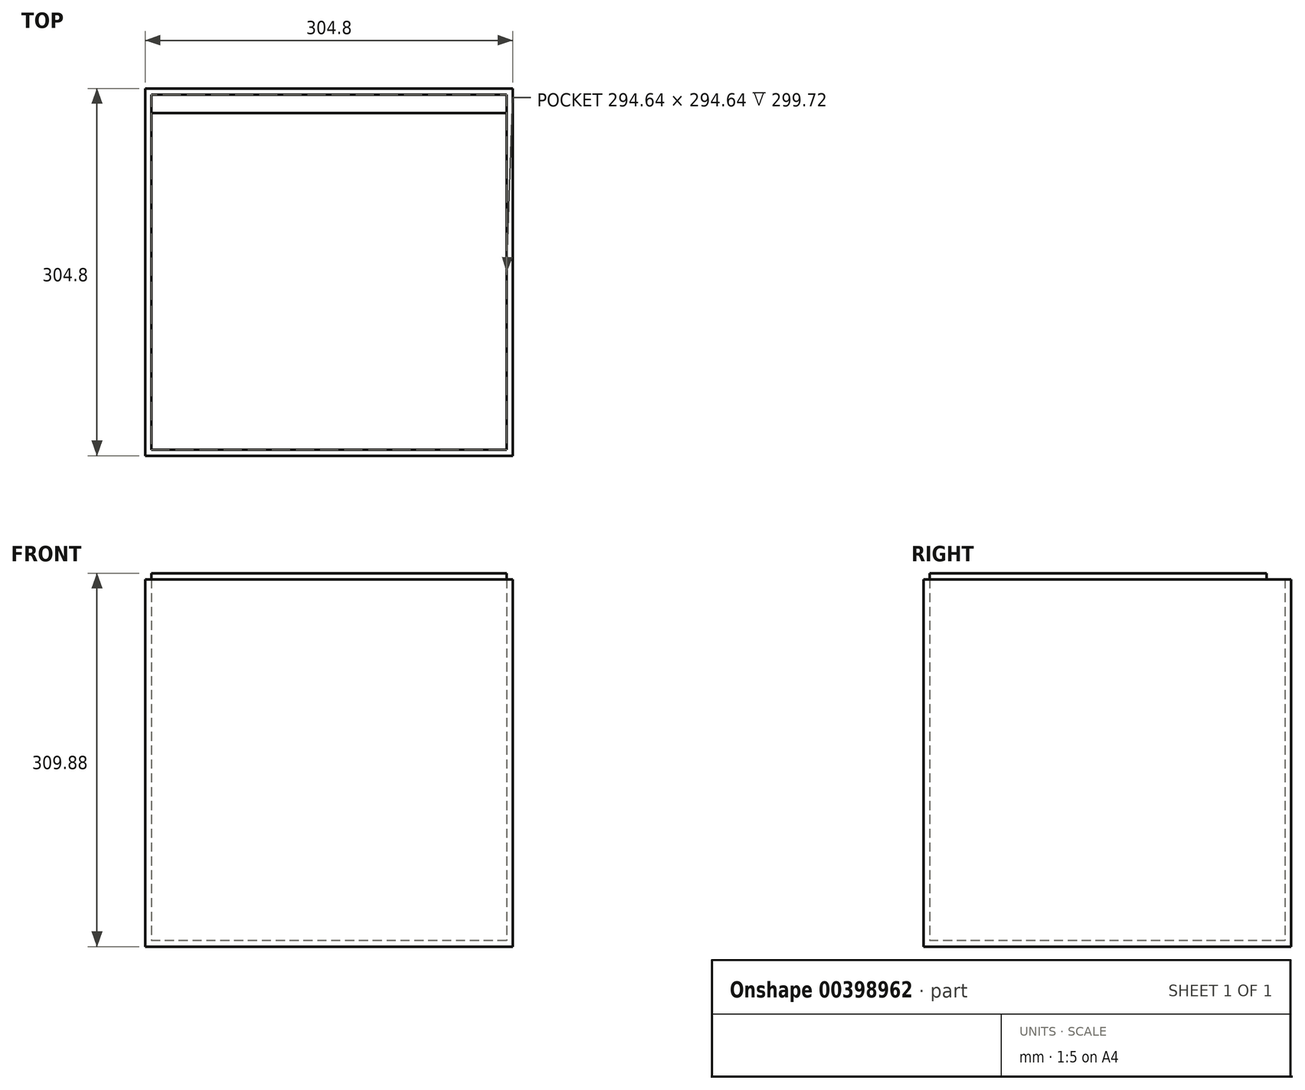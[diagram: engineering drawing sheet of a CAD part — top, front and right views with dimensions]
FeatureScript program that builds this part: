
annotation { "Feature Type Name" : "Feature", "Feature Type Description" : "" }
export const myFeature = defineFeature(function(context is Context, id is Id, definition is map)
    precondition{}
    {
        {
            var Q0;
            Q0=qCreatedBy(makeId("Top.planeOp"),FACE);
            var sketch = newSketch(context, id + "F0", { "sketchPlane" : qUnion([Q0])});
            skLineSegment(sketch, "E0.bottom", {"start": v(152.4, 152.4) * mm, "end": v(-152.4, 152.4) * mm});
            skLineSegment(sketch, "E0.top", {"start": v(152.4, -152.4) * mm, "end": v(-152.4, -152.4) * mm});
            skLineSegment(sketch, "E0.left", {"start": v(152.4, 152.4) * mm, "end": v(152.4, -152.4) * mm});
            skLineSegment(sketch, "E0.right", {"start": v(-152.4, 152.4) * mm, "end": v(-152.4, -152.4) * mm});
            skPoint(sketch, "E0.middle", {"position": v(0, 0) * mm});
            skSolve(sketch);
        }
        {
            var Q0;
            Q0 = qSketchRegion(id + "F0", true);
            extrude(context, id + "F1", {"entities" : qUnion([Q0]), "depth" : 304.8 * mm, "symmetric" : true});
        }
        {
            var Q0;
            Q0=makeQuery(id+"F1.opExtrude","CAP_FACE",FACE,{"disambiguationData":[OSD([sQuery(id+"F0.wireOp",EDGE,"E0.bottom"),sQuery(id+"F0.wireOp",EDGE,"E0.top"),sQuery(id+"F0.wireOp",EDGE,"E0.left"),sQuery(id+"F0.wireOp",EDGE,"E0.right")])],"isStart":false});
            shell(context, id + "F2", {"entities" : qUnion([Q0]), "thickness" : 5.08 * mm});
        }
        {
            var Q0;
            Q0=makeQuery(id+"F2.opShell","OFFSET_FACE",FACE,{"disambiguationData":[OSD([sQuery(id+"F0.wireOp",EDGE,"E0.top")])]});
            var sketch = newSketch(context, id + "F3", { "sketchPlane" : qUnion([Q0])});
            skLineSegment(sketch, "E1.bottom", {"start": v(147.32, 152.4) * mm, "end": v(-147.32, 152.4) * mm});
            skLineSegment(sketch, "E1.top", {"start": v(147.32, 157.48) * mm, "end": v(-147.32, 157.48) * mm});
            skLineSegment(sketch, "E1.left", {"start": v(147.32, 152.4) * mm, "end": v(147.32, 157.48) * mm});
            skLineSegment(sketch, "E1.right", {"start": v(-147.32, 152.4) * mm, "end": v(-147.32, 157.48) * mm});
            skSolve(sketch);
        }
        {
            var Q0;
            Q0 = qSketchRegion(id + "F3", true);
            extrude(context, id + "F4", {"entities" : qUnion([Q0]), "depth" : 279.4 * mm});
        }
    });
